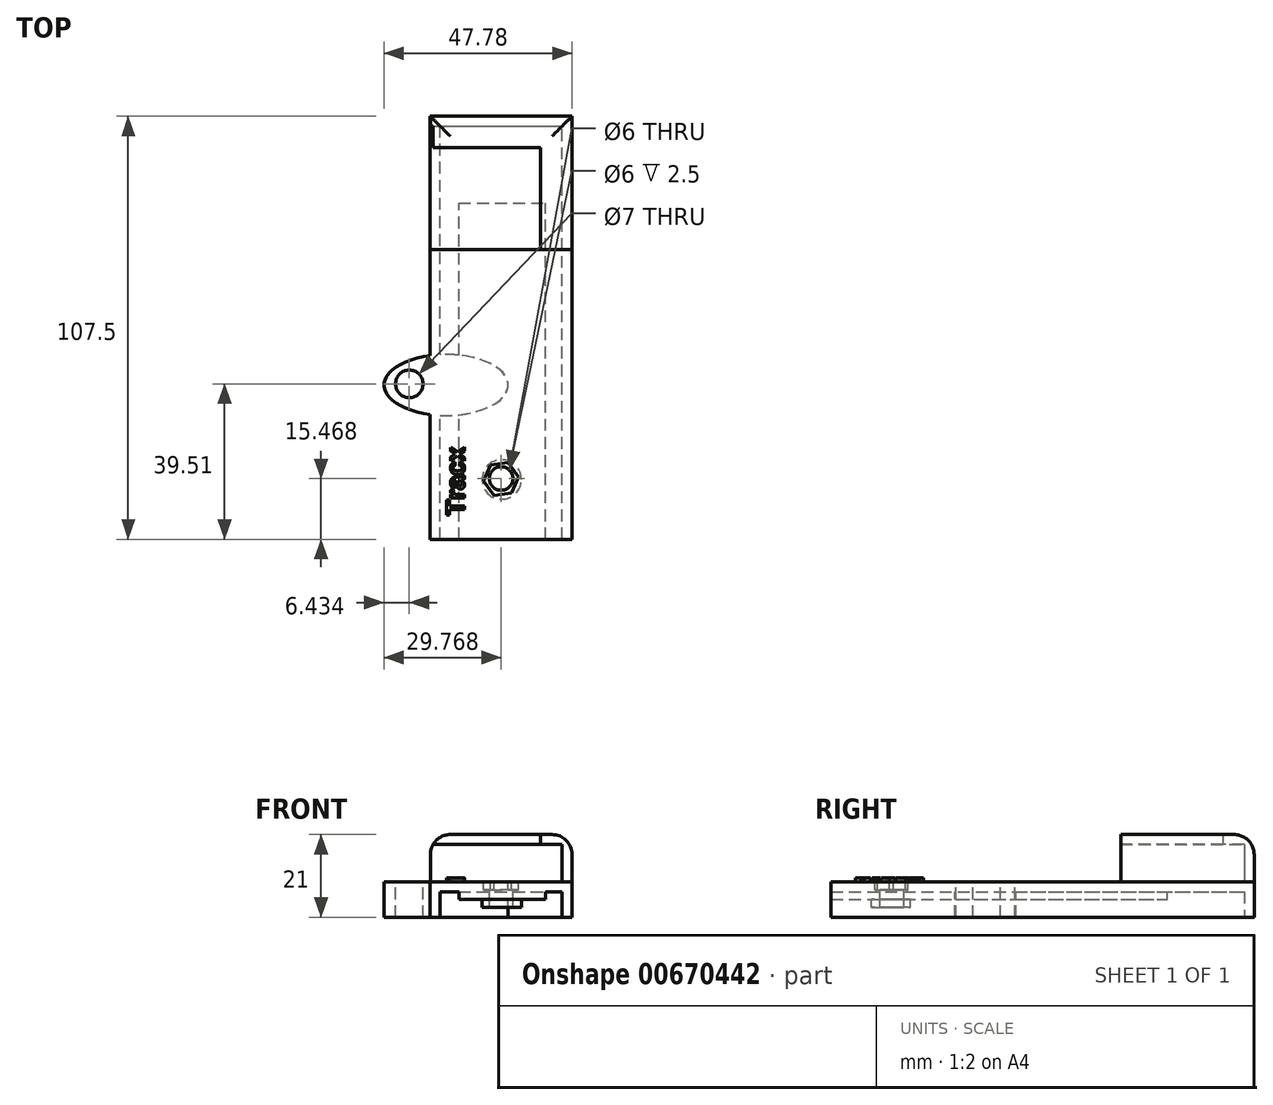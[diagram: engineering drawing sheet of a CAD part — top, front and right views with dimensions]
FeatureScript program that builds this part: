
annotation { "Feature Type Name" : "Feature", "Feature Type Description" : "" }
export const myFeature = defineFeature(function(context is Context, id is Id, definition is map)
    precondition{}
    {
        {
            var Q0;
            Q0=qCreatedBy(makeId("Front.planeOp"),FACE);
            cPlane(context, id + "F0", {"entities" : qUnion([Q0]), "cplaneType" : CPlaneType.OFFSET, "offset" : 55 * mm, "oppositeDirection" : true, "width" : 152.4 * mm, "height" : 152.4 * mm});
        }
        {
            var Q0;
            Q0=qCreatedBy(makeId("Front.planeOp"),FACE);
            var sketch = newSketch(context, id + "F1", { "sketchPlane" : qUnion([Q0])});
            skLineSegment(sketch, "E0.bottom", {"start": v(-15.93, 5.18) * mm, "end": v(20.07, 5.18) * mm});
            skLineSegment(sketch, "E0.top", {"start": v(-15.93, -3.82) * mm, "end": v(20.07, -3.82) * mm});
            skLineSegment(sketch, "E0.left", {"start": v(-15.93, 5.18) * mm, "end": v(-15.93, -3.82) * mm});
            skLineSegment(sketch, "E0.right", {"start": v(20.07, 5.18) * mm, "end": v(20.07, -3.82) * mm});
            skSolve(sketch);
        }
        {
            var Q0;
            Q0=qCreatedBy(id+"F0.planeOp",FACE);
            var sketch = newSketch(context, id + "F2", { "sketchPlane" : qUnion([Q0])});
            skLineSegment(sketch, "E1.bottom", {"start": v(-15.92, 17.18) * mm, "end": v(20.08, 17.18) * mm});
            skLineSegment(sketch, "E1.top", {"start": v(-15.92, 5.18) * mm, "end": v(20.08, 5.18) * mm});
            skLineSegment(sketch, "E1.left", {"start": v(-15.92, 17.18) * mm, "end": v(-15.92, 5.18) * mm});
            skLineSegment(sketch, "E1.right", {"start": v(20.08, 17.18) * mm, "end": v(20.08, 5.18) * mm});
            skSolve(sketch);
        }
        {
            var Q0;
            Q0=makeQuery(id+"F2.imprint","IMPRINT",FACE,{"disambiguationData":[TD([[makeQuery(id+"F2.imprint","IMPRINT",EDGE,{"derivedFrom":sQuery(id+"F2.wireOp",EDGE,"E1.bottom")}),-1.0]])]});
            extrude(context, id + "F3", {"entities" : qUnion([Q0]), "depth" : 36 * mm, "offsetDistance" : 25.4 * mm});
        }
        {
            var Q0;
            Q0=makeQuery(id+"F1.imprint","IMPRINT",FACE,{"disambiguationData":[TD([[makeQuery(id+"F1.imprint","IMPRINT",EDGE,{"derivedFrom":sQuery(id+"F1.wireOp",EDGE,"E0.bottom")}),-1.0]])]});
            extrude(context, id + "F4", {"entities" : qUnion([Q0]), "endBound" : BoundingType.SYMMETRIC, "depth" : 110 * mm, "offsetDistance" : 25.4 * mm});
        }
        {
            var Q0;
            Q0=makeQuery(id+"F4.opExtrude","SWEPT_FACE",FACE,{"disambiguationData":[OSD([sQuery(id+"F1.wireOp",EDGE,"E0.bottom")])]});
            var sketch = newSketch(context, id + "F5", { "sketchPlane" : qUnion([Q0])});
            skCircle(sketch, "E2.cCircle", {"center": v(2.07, -37.16) * mm, "radius": 4.5 * mm, "construction": true});
            skLineSegment(sketch, "E2.0", {"start": v(4.77, -40.76) * mm, "end": v(0.3, -41.3) * mm});
            skLineSegment(sketch, "E2.1", {"start": v(0.3, -41.3) * mm, "end": v(-2.4, -37.7) * mm});
            skLineSegment(sketch, "E2.2", {"start": v(-2.4, -37.7) * mm, "end": v(-0.63, -33.56) * mm});
            skLineSegment(sketch, "E2.3", {"start": v(-0.63, -33.56) * mm, "end": v(3.84, -33.02) * mm});
            skLineSegment(sketch, "E2.4", {"start": v(3.84, -33.02) * mm, "end": v(6.54, -36.62) * mm});
            skLineSegment(sketch, "E2.5", {"start": v(6.54, -36.62) * mm, "end": v(4.77, -40.76) * mm});
            skSolve(sketch);
        }
        {
            var Q0;
            Q0=makeQuery(id+"F5.imprint","IMPRINT",FACE,{"disambiguationData":[TD([[makeQuery(id+"F5.imprint","IMPRINT",EDGE,{"derivedFrom":sQuery(id+"F5.wireOp",EDGE,"E2.0")}),-1.0]])]});
            extrude(context, id + "F6", {"entities" : qUnion([Q0]), "operationType" : NewBodyOperationType.REMOVE, "oppositeDirection" : true, "depth" : 2 * mm, "offsetDistance" : 25.4 * mm});
        }
        {
            var Q0;
            Q0=makeQuery(id+"F4.opExtrude","SWEPT_FACE",FACE,{"disambiguationData":[OSD([sQuery(id+"F1.wireOp",EDGE,"E0.top")])]});
            shell(context, id + "F7", {"entities" : qUnion([Q0]), "thickness" : 2.5 * mm});
        }
        {
            var Q0;
            Q0=makeQuery(id+"F4.opExtrude","CAP_FACE",FACE,{"disambiguationData":[OSD([sQuery(id+"F1.wireOp",EDGE,"E0.bottom"),sQuery(id+"F1.wireOp",EDGE,"E0.top"),sQuery(id+"F1.wireOp",EDGE,"E0.left"),sQuery(id+"F1.wireOp",EDGE,"E0.right")])],"isStart":false});
            extrude(context, id + "F8", {"entities" : qUnion([Q0]), "operationType" : NewBodyOperationType.REMOVE, "oppositeDirection" : true, "depth" : 2.5 * mm, "offsetDistance" : 25.4 * mm});
        }
        {
            var Q0;
            Q0=makeQuery(id+"F7.opShell","OFFSET_FACE",FACE,{"disambiguationData":[OSD([sQuery(id+"F5.wireOp",EDGE,"E2.0"),sQuery(id+"F5.wireOp",EDGE,"E2.1"),sQuery(id+"F5.wireOp",EDGE,"E2.2"),sQuery(id+"F5.wireOp",EDGE,"E2.3"),sQuery(id+"F5.wireOp",EDGE,"E2.4"),sQuery(id+"F5.wireOp",EDGE,"E2.5")])]});
            extrude(context, id + "F9", {"entities" : qUnion([Q0]), "operationType" : NewBodyOperationType.REMOVE, "oppositeDirection" : true, "depth" : 2 * mm, "offsetDistance" : 25.4 * mm});
        }
        {
            var Q0;
            Q0=makeQuery(id+"F9.boolean.opBoolean","MERGE",FACE,{"derivedFrom":[makeQuery(id+"F7.opShell","OFFSET_FACE",FACE,{"disambiguationData":[OSD([sQuery(id+"F1.wireOp",EDGE,"E0.bottom")])]}),makeQuery(id+"F9.opExtrude","CAP_FACE",FACE,{"disambiguationData":[OSD([sQuery(id+"F5.wireOp",EDGE,"E2.0"),sQuery(id+"F5.wireOp",EDGE,"E2.1"),sQuery(id+"F5.wireOp",EDGE,"E2.2"),sQuery(id+"F5.wireOp",EDGE,"E2.3"),sQuery(id+"F5.wireOp",EDGE,"E2.4"),sQuery(id+"F5.wireOp",EDGE,"E2.5")])],"isStart":false})]});
            var sketch = newSketch(context, id + "F10", { "sketchPlane" : qUnion([Q0])});
            skLineSegment(sketch, "E3.bottom", {"start": v(-8.66, 52.5) * mm, "end": v(13.34, 52.5) * mm});
            skLineSegment(sketch, "E3.top", {"start": v(-8.66, -32.96) * mm, "end": v(13.34, -32.96) * mm});
            skLineSegment(sketch, "E3.left", {"start": v(-8.66, 52.5) * mm, "end": v(-8.66, -32.96) * mm});
            skLineSegment(sketch, "E3.right", {"start": v(13.34, 52.5) * mm, "end": v(13.34, -32.96) * mm});
            skSolve(sketch);
        }
        {
            var Q0;
            Q0=makeQuery(id+"F10.imprint","IMPRINT",FACE,{"disambiguationData":[TD([[makeQuery(id+"F10.imprint","IMPRINT",EDGE,{"derivedFrom":sQuery(id+"F10.wireOp",EDGE,"E3.bottom")}),-1.0]])]});
            extrude(context, id + "F11", {"entities" : qUnion([Q0]), "operationType" : NewBodyOperationType.ADD, "depth" : 2 * mm, "offsetDistance" : 25.4 * mm});
        }
        {
            var Q0;
            Q0=makeQuery(id+"F11.opExtrude","CAP_FACE",FACE,{"disambiguationData":[OSD([sQuery(id+"F10.wireOp",EDGE,"E3.bottom"),sQuery(id+"F10.wireOp",EDGE,"E3.top"),sQuery(id+"F10.wireOp",EDGE,"E3.left"),sQuery(id+"F10.wireOp",EDGE,"E3.right")])],"isStart":false});
            var sketch = newSketch(context, id + "F12", { "sketchPlane" : qUnion([Q0])});
            skCircle(sketch, "E4", {"center": v(2.2, 37.3) * mm, "radius": 5 * mm});
            skSolve(sketch);
        }
        {
            var Q0;
            Q0=makeQuery(id+"F12.imprint","IMPRINT",FACE,{"disambiguationData":[TD([[makeQuery(id+"F12.imprint","IMPRINT",EDGE,{"derivedFrom":sQuery(id+"F12.wireOp",EDGE,"E4")}),1.0]])]});
            extrude(context, id + "F13", {"entities" : qUnion([Q0]), "depth" : 2 * mm, "offsetDistance" : 25.4 * mm});
        }
        {
            var Q0;
            Q0=makeQuery(id+"F5.imprint","IMPRINT",FACE,{"disambiguationData":[TD([[makeQuery(id+"F5.imprint","IMPRINT",EDGE,{"derivedFrom":sQuery(id+"F5.wireOp",EDGE,"E2.0")}),-1.0]])]});
            var sketch = newSketch(context, id + "F14", { "sketchPlane" : qUnion([Q0])});
            skCircle(sketch, "E5", {"center": v(2.07, -37.03) * mm, "radius": 1.76 * mm});
            skSolve(sketch);
        }
        {
            var Q0;
            Q0=sQuery(id+"F14.wireOp",VERTEX,"E5.center");
            var Q1;
            Q1=makeQuery(id+"F4.opExtrude","SWEPT_BODY",BODY,{"disambiguationData":[OSD([sQuery(id+"F1.wireOp",EDGE,"E0.bottom"),sQuery(id+"F1.wireOp",EDGE,"E0.top"),sQuery(id+"F1.wireOp",EDGE,"E0.left"),sQuery(id+"F1.wireOp",EDGE,"E0.right")])]});
            var Q2;
            Q2=makeQuery(id+"F13.opExtrude","SWEPT_BODY",BODY,{"disambiguationData":[OSD([sQuery(id+"F12.wireOp",EDGE,"E4")])]});
            hole(context, id + "F15", {"style" : HoleStyle.SIMPLE, "endStyle" : HoleEndStyle.BLIND, "holeDiameter" : 6 * mm, "majorDiameter" : 6.35 * mm, "holeDepth" : 12.7 * mm, "isTappedThrough" : true, "tappedDepth" : 12.7 * mm, "tapClearance" : 3, "locations" : qUnion([Q0]), "scope" : qUnion([Q1, Q2])});
        }
        {
            var Q0;
            Q0=makeQuery(id+"F3.opExtrude","CAP_FACE",FACE,{"disambiguationData":[OSD([sQuery(id+"F2.wireOp",EDGE,"E1.bottom"),sQuery(id+"F2.wireOp",EDGE,"E1.top"),sQuery(id+"F2.wireOp",EDGE,"E1.left"),sQuery(id+"F2.wireOp",EDGE,"E1.right")])],"isStart":false});
            extrude(context, id + "F16", {"entities" : qUnion([Q0]), "operationType" : NewBodyOperationType.REMOVE, "oppositeDirection" : true, "depth" : 2.1 * mm, "offsetDistance" : 25.4 * mm});
        }
        {
            var Q0;
            Q0=makeQuery(id+"F5.imprint","IMPRINT",FACE,{"disambiguationData":[TD([[makeQuery(id+"F5.imprint","IMPRINT",EDGE,{"derivedFrom":sQuery(id+"F5.wireOp",EDGE,"E2.0")}),1.0]])]});
            var sketch = newSketch(context, id + "F17", { "sketchPlane" : qUnion([Q0])});
            skEllipse(sketch, "E6", {"center": v(-11.93, -13.27) * mm, "majorRadius": 15.77 * mm, "minorRadius": 7.74 * mm, "majorAxis": v(1, 0)});
            skPoint(sketch, "E7", {"position": v(3.84, -13.27) * mm});
            skSolve(sketch);
        }
        {
            var Q0;
            {var subQ0=sQuery(id+"F17.wireOp",EDGE,"E6");var subQ1=makeQuery(id+"F5.imprint","IMPRINT",EDGE,{"derivedFrom":makeQuery(id+"F4.opExtrude","SWEPT_EDGE",EDGE,{"disambiguationData":[OSD([sQuery(id+"F1.wireOp",EDGE,"E0.bottom"),sQuery(id+"F1.wireOp",EDGE,"E0.right")])]})});var subQ2=makeQuery(id+"F17.imprint","INTERSECT",VERTEX,{"disambiguationData":[OD(0.0)],"derivedFrom":[subQ1,subQ0]});Q0=makeQuery(id+"F17.imprint","IMPRINT",FACE,{"disambiguationData":[TD([[makeQuery(id+"F17.imprint","IMPRINT",EDGE,{"disambiguationData":[TD([[subQ2,1.0]])],"derivedFrom":subQ0}),1.0]])]});}
            var Q1;
            {var subQ0=sQuery(id+"F17.wireOp",EDGE,"E6");var subQ1=makeQuery(id+"F5.imprint","IMPRINT",EDGE,{"derivedFrom":makeQuery(id+"F4.opExtrude","SWEPT_EDGE",EDGE,{"disambiguationData":[OSD([sQuery(id+"F1.wireOp",EDGE,"E0.bottom"),sQuery(id+"F1.wireOp",EDGE,"E0.left")])]})});var subQ2=makeQuery(id+"F17.imprint","INTERSECT",VERTEX,{"disambiguationData":[OD(0.0)],"derivedFrom":[subQ1,subQ0]});Q1=makeQuery(id+"F17.imprint","IMPRINT",FACE,{"disambiguationData":[TD([[makeQuery(id+"F17.imprint","IMPRINT",EDGE,{"disambiguationData":[TD([[subQ2,-1.0]])],"derivedFrom":subQ0}),1.0]])]});}
            extrude(context, id + "F18", {"entities" : qUnion([Q0, Q1]), "operationType" : NewBodyOperationType.ADD, "oppositeDirection" : true, "depth" : 9 * mm, "offsetDistance" : 25.4 * mm});
        }
        {
            var Q0;
            {var subQ0=sQuery(id+"F1.wireOp",EDGE,"E0.bottom");Q0=makeQuery(id+"F18.boolean.opBoolean","MERGE",FACE,{"derivedFrom":[makeQuery(id+"F4.opExtrude","SWEPT_FACE",FACE,{"disambiguationData":[OSD([subQ0])]}),makeQuery(id+"F18.opExtrude","CAP_FACE",FACE,{"disambiguationData":[OSD([subQ0,sQuery(id+"F1.wireOp",EDGE,"E0.right"),sQuery(id+"F17.wireOp",EDGE,"E6")])],"isStart":true})]});}
            var sketch = newSketch(context, id + "F19", { "sketchPlane" : qUnion([Q0])});
            skCircle(sketch, "E8", {"center": v(-21.27, -13) * mm, "radius": 3.5 * mm});
            skSolve(sketch);
        }
        {
            var Q0;
            Q0=makeQuery(id+"F19.imprint","IMPRINT",FACE,{"disambiguationData":[TD([[makeQuery(id+"F19.imprint","IMPRINT",EDGE,{"derivedFrom":sQuery(id+"F19.wireOp",EDGE,"E8")}),1.0]])]});
            extrude(context, id + "F20", {"entities" : qUnion([Q0]), "operationType" : NewBodyOperationType.REMOVE, "oppositeDirection" : true, "depth" : 25.4 * mm, "offsetDistance" : 25.4 * mm});
        }
        {
            var Q0;
            Q0=makeQuery(id+"F3.opExtrude","SWEPT_FACE",FACE,{"disambiguationData":[OSD([sQuery(id+"F2.wireOp",EDGE,"E1.left")])]});
            var Q1;
            Q1=makeQuery(id+"F16.boolean.opBoolean","COPY",FACE,{"derivedFrom":makeQuery(id+"F16.opExtrude","CAP_FACE",FACE,{"disambiguationData":[OSD([sQuery(id+"F2.wireOp",EDGE,"E1.bottom"),sQuery(id+"F2.wireOp",EDGE,"E1.top"),sQuery(id+"F2.wireOp",EDGE,"E1.left"),sQuery(id+"F2.wireOp",EDGE,"E1.right")])],"isStart":false})});
            shell(context, id + "F21", {"entities" : qUnion([Q0, Q1]), "thickness" : 2.54 * mm});
        }
        {
            var Q0;
            Q0=makeQuery(id+"F21.opShell","OFFSET_FACE",FACE,{"disambiguationData":[OSD([sQuery(id+"F2.wireOp",EDGE,"E1.top")])]});
            extrude(context, id + "F22", {"entities" : qUnion([Q0]), "operationType" : NewBodyOperationType.REMOVE, "oppositeDirection" : true, "depth" : 2.7 * mm, "offsetDistance" : 25.4 * mm});
        }
        {
            var Q0;
            Q0=makeQuery(id+"F21.opShell","OFFSET_FACE",FACE,{"disambiguationData":[OSD([sQuery(id+"F2.wireOp",EDGE,"E1.bottom")])]});
            var Q1;
            Q1=makeQuery(id+"F3.opExtrude","SWEPT_FACE",FACE,{"disambiguationData":[OSD([sQuery(id+"F2.wireOp",EDGE,"E1.bottom")])]});
            var Q2;
            Q2=makeQuery(id+"F16.boolean.opBoolean","COPY",FACE,{"derivedFrom":makeQuery(id+"F16.opExtrude","CAP_FACE",FACE,{"disambiguationData":[OSD([sQuery(id+"F2.wireOp",EDGE,"E1.bottom"),sQuery(id+"F2.wireOp",EDGE,"E1.top"),sQuery(id+"F2.wireOp",EDGE,"E1.left"),sQuery(id+"F2.wireOp",EDGE,"E1.right")])],"isStart":false})});
            var Q3;
            Q3=makeQuery(id+"F3.opExtrude","SWEPT_FACE",FACE,{"disambiguationData":[OSD([sQuery(id+"F2.wireOp",EDGE,"E1.left")])]});
            shell(context, id + "F23", {"entities" : qUnion([Q0, Q1, Q2, Q3]), "thickness" : 8 * mm});
        }
        {
            var Q0;
            Q0=makeQuery(id+"F16.boolean.opBoolean","COPY",EDGE,{"derivedFrom":makeQuery(id+"F16.opExtrude","CAP_EDGE",EDGE,{"disambiguationData":[OSD([sQuery(id+"F2.wireOp",EDGE,"E1.bottom")])],"isStart":false})});
            var Q1;
            Q1=makeQuery(id+"F3.opExtrude","SWEPT_EDGE",EDGE,{"disambiguationData":[OSD([sQuery(id+"F2.wireOp",EDGE,"E1.bottom"),sQuery(id+"F2.wireOp",EDGE,"E1.left")])]});
            fillet(context, id + "F24", {"entities" : qUnion([Q0, Q1]), "radius" : 5.08 * mm, "tangentPropagation" : true, "allowEdgeOverflow" : false});
        }
        {
            var Q0;
            Q0=makeQuery(id+"F5.imprint","IMPRINT",FACE,{"disambiguationData":[TD([[makeQuery(id+"F5.imprint","IMPRINT",EDGE,{"derivedFrom":sQuery(id+"F5.wireOp",EDGE,"E2.0")}),1.0]])]});
            var sketch = newSketch(context, id + "F25", { "sketchPlane" : qUnion([Q0])});
            skText(sketch, "E9", { "text": "Tracx", "fontName": "Arimo-Bold.ttf"});
            const initialGuessF25  = {"E9": [-0.00728, -0.04642, 0, 1, 0.0047]};
            skSetInitialGuess(sketch, initialGuessF25);
            skSolve(sketch);
        }
        {
            var Q0;
            Q0 = qSketchRegion(id + "F25", true);
            extrude(context, id + "F26", {"entities" : qUnion([Q0]), "operationType" : NewBodyOperationType.ADD, "depth" : 1 * mm, "offsetDistance" : 25.4 * mm});
        }
        {
            var Q0;
            Q0=makeQuery(id+"F3.opExtrude","SWEPT_EDGE",EDGE,{"disambiguationData":[OSD([sQuery(id+"F2.wireOp",EDGE,"E1.bottom"),sQuery(id+"F2.wireOp",EDGE,"E1.right")])]});
            var Q1;
            Q1=makeQuery(id+"F3.opExtrude","CAP_EDGE",EDGE,{"disambiguationData":[OSD([sQuery(id+"F2.wireOp",EDGE,"E1.bottom")])],"isStart":true});
            fillet(context, id + "F27", {"entities" : qUnion([Q0, Q1]), "radius" : 5.08 * mm, "tangentPropagation" : true, "allowEdgeOverflow" : false});
        }
    });
